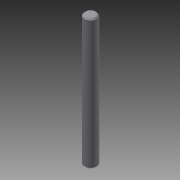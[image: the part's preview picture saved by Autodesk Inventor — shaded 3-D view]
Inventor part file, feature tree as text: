
AUTODESK INVENTOR PART (.ipt)
format: ipt  version: 2015 (Build 190159000, 159)  size: 82,944 bytes
history: native  units: in
note: dims shown in document units (in); Inventor stores cm internally (conversion verified against a paired STEP export)
features: other x3, extrude x1, chamfer x1, sketch x1
ambient origin geometry x8: Origin, YZ Plane, XZ Plane, XY Plane, X Axis, Y Axis, Z Axis, Center Point
bodies: Solid1 (feature_tree)
feature tree (6):
  other  "Axle-100mm - 739088.ipt"
  extrude  "Extrusion1"  Depth=1.9685in TaperAngle=0.0deg
  chamfer  "Chamfer1"  Distance=0.0197in Angle=45.0deg
  other  "tetrix_739088_2013::Axle-100mm - 739088.ipt"
  other  "TaggingFeature1"
  sketch  "Sketch1"  dims[d0=0.3937in d1=1.9685in d2=0.0in d3=0.0197in d4=0.125in d5=45.0deg]
